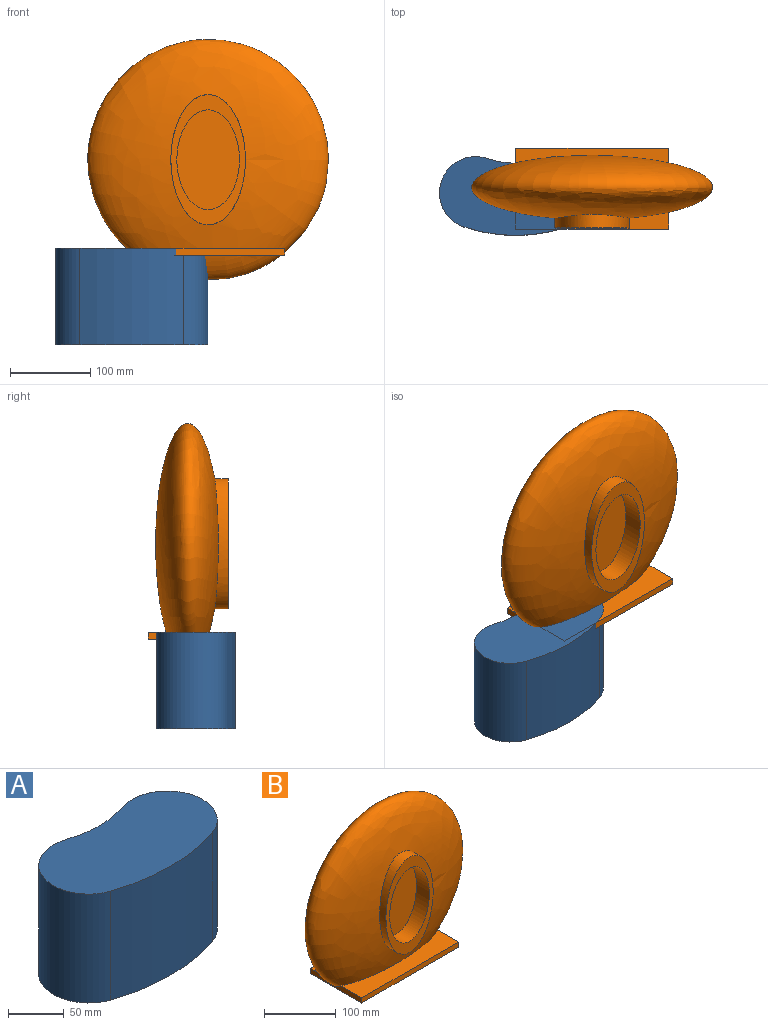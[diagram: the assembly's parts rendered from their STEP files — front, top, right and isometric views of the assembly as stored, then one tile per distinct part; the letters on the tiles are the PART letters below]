
ASSEMBLY  parts=2 mates=1
PART A: 6 faces, bbox 190x98.3x120 mm
  f0: cylinder r=45mm len=120mm, axis (0,0,-1), area 16964.6mm2, adj f1,f3,f4,f5
  f1: cylinder r=200mm len=129.03mm, axis (0,0,-1), area 15765.8mm2, adj f0,f2,f4,f5
  f2: cylinder r=45mm len=120mm, axis (0,0,-1), area 16964.6mm2, adj f1,f3,f4,f5
  f3: cylinder r=110mm len=120mm, axis (0,0,-1), area 8671.2mm2, adj f0,f2,f4,f5
  f4: plane 190x98.29mm, normal (0,0,1), area 15525.6mm2, adj f0,f1,f2,f3
  f5: plane 190x98.29mm, normal (0,0,-1), area 15525.6mm2, adj f0,f1,f2,f3
PART B: 13 faces, bbox 299.9x100.6x300 mm
  f0: extruded ~124.31x77.93mm, area 8175.6mm2, adj f2,f4
  f1: extruded ~162.21x92.87mm, area 5808.8mm2, adj f2,f3
  f2: plane 162.21x92.87mm, normal (0,-1,0), area 4222.6mm2, adj f0,f1
  f3: revolved ~299.94x299.94mm, area 135202mm2, adj f1,f5,f6,f10,f11
  f4: plane 124.31x77.93mm, normal (0,-1,0), area 7608.8mm2, adj f0
  f5: plane 190.5x42.12mm, normal (0,0,1), area 5580.8mm2, adj f3,f7,f10,f11
  f6: plane 190.5x39.53mm, normal (0,0,1), area 5088.2mm2, adj f3,f9,f10,f11
  f7: plane 190.5x8.66mm, normal (0,-1,0), area 1649.4mm2, adj f5,f8,f10,f11
  f8: plane 190.5x100.6mm, normal (0,0,-1), area 12188.4mm2, adj f7,f9,f10,f11,f12
  f9: plane 190.5x8.66mm, normal (0,1,0), area 1649.4mm2, adj f6,f8,f10,f11
  f10: plane 100.6x8.66mm, normal (1,0,0), area 800.1mm2, adj f3,f5,f6,f7,f8,f9
  f11: plane 100.6x8.66mm, normal (-1,0,0), area 800.1mm2, adj f3,f5,f6,f7,f8,f9
  f12: revolved ~182.78x55.68mm, area 11316mm2, adj f8
PLACE A t=(-118.81,103.37,-25.45)mm
PLACE B t=(-23.56,88.94,204.85)mm
MATE fastened A.f4 <-> B.f5  axis (0,0,1) through (-118.81,104.46,94.55)mm
